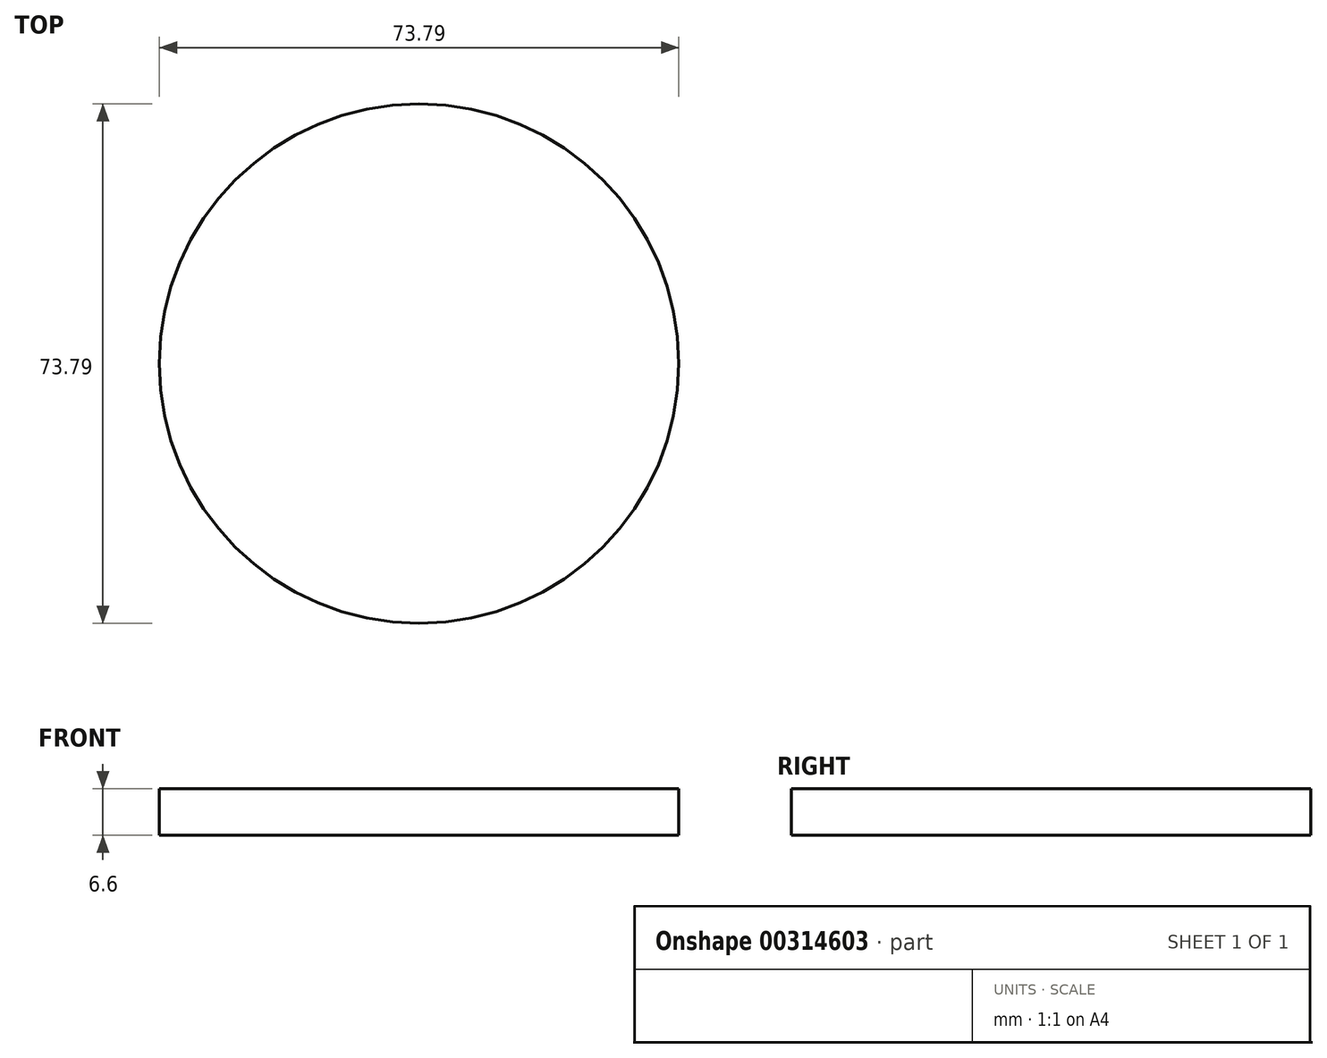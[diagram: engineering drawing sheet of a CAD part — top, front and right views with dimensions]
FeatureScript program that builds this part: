
annotation { "Feature Type Name" : "Feature", "Feature Type Description" : "" }
export const myFeature = defineFeature(function(context is Context, id is Id, definition is map)
    precondition{}
    {
        {
            var Q0;
            Q0=qCreatedBy(makeId("Top.planeOp"),FACE);
            var sketch = newSketch(context, id + "F0", { "sketchPlane" : qUnion([Q0])});
            skCircle(sketch, "E0", {"center": v(-53.22, 23.76) * mm, "radius": 36.9 * mm});
            skSolve(sketch);
        }
        {
            var Q0;
            Q0 = qSketchRegion(id + "F0", true);
            extrude(context, id + "F1", {"entities" : qUnion([Q0]), "depth" : 6.6 * mm});
        }
    });
